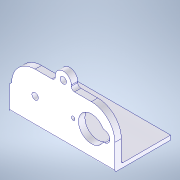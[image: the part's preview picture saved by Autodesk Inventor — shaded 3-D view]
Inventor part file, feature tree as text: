
AUTODESK INVENTOR PART (.ipt)
format: ipt  version: 2022 (Build 260153000, 153)  size: 186,368 bytes
history: native  units: in
note: dims shown in document units (in); Inventor stores cm internally (conversion verified against a paired STEP export)
features: extrude x4, sketch x4, fillet x3, direct_edit x1, move_body x1
ambient origin geometry x8: Origin, YZ Plane, XZ Plane, XY Plane, X Axis, Y Axis, Z Axis, Center Point
bodies: Solid1 (feature_tree)
feature tree (13):
  extrude  "Extrusion1"  Depth=0.1181in TaperAngle=0.0deg
  fillet  "Fillet1"  Radius=0.0591in
  fillet  "Fillet2"  Radius=0.0591in
  extrude  "Extrusion2"  Depth=0.0315in
  fillet  "Fillet3"  Radius=0.0669in
  extrude  "Extrusion5"  Depth=1.172in
  direct_edit  "Direct Edit3"
  extrude  "Extrusion8"  TaperAngle=0.0deg  [1 undecoded]
  sketch  "Sketch1"  dims[d0=0.1181in d1=0.2953in d2=0.1181in d3=0.0in d4=0.0591in d5=0.0591in]
  sketch  "Sketch2"  dims[d11=0.9055in d12=0.0in d19=0.0315in d20=0.0669in]
  sketch  "Sketch5"  dims[d21=0.515in d22=1.172in]
  sketch  "Sketch10"  dims[d23=1.0236in d24=0.0in d43=0.0in d44=0.0in d45=-0.0394in d47=0.0039in d48=0.0394in d49=0.0in]
  move_body  "Move3"
note: 1 required parameter value undecoded (feature->parameter linkage not recoverable at this tier; creation-order binding heuristic only, values carry confidence <= 0.55)
